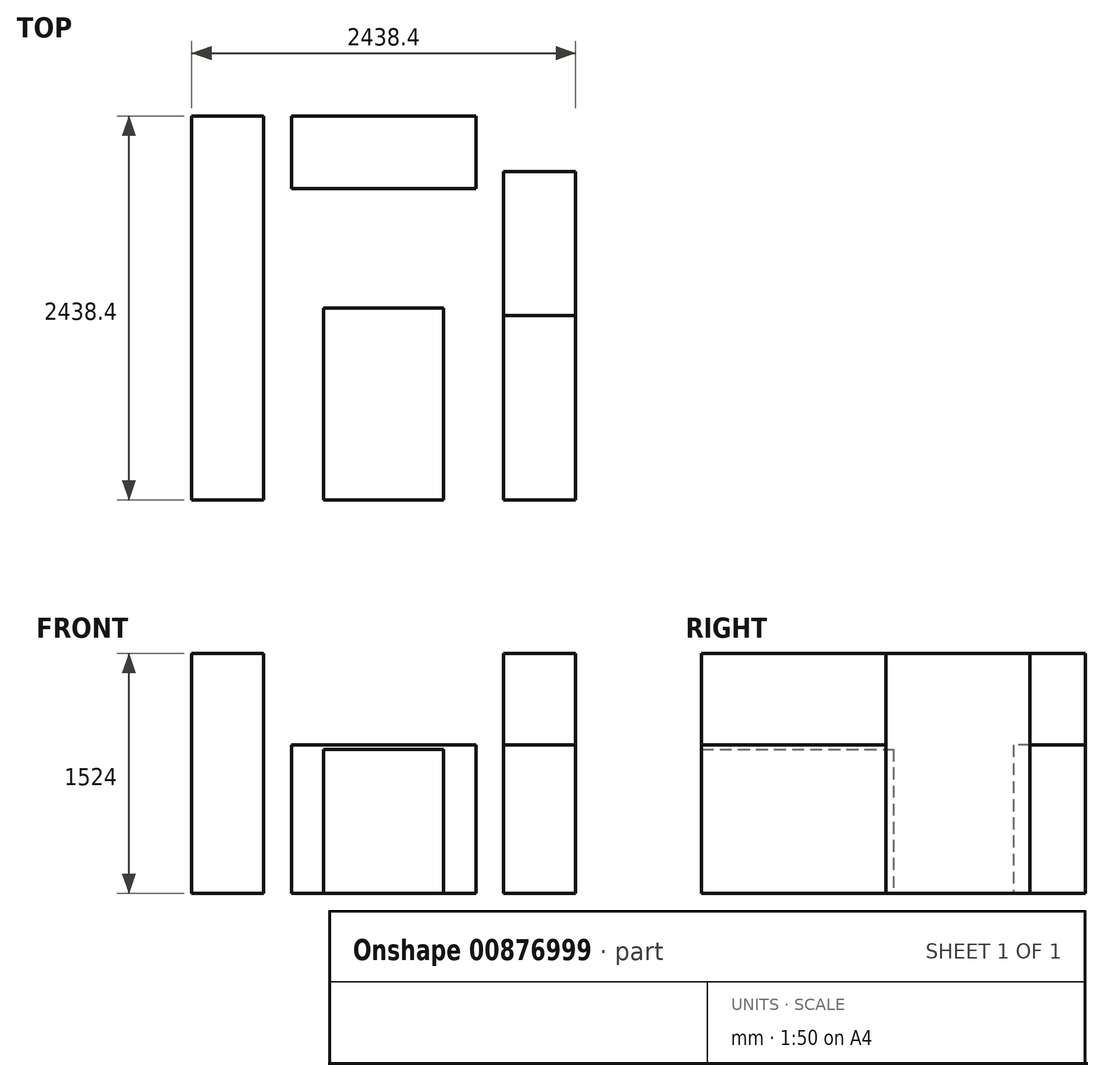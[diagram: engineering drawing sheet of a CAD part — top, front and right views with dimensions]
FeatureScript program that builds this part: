
annotation { "Feature Type Name" : "Feature", "Feature Type Description" : "" }
export const myFeature = defineFeature(function(context is Context, id is Id, definition is map)
    precondition{}
    {
        {
            var Q0;
            Q0=qCreatedBy(makeId("Top.planeOp"),FACE);
            var sketch = newSketch(context, id + "F0", { "sketchPlane" : qUnion([Q0])});
            skLineSegment(sketch, "E0", {"start": v(0, 0) * mm, "end": v(-2438.4, 0) * mm, "construction": true});
            skLineSegment(sketch, "E1.bottom", {"start": v(-2438.4, 0) * mm, "end": v(-1981.2, 0) * mm});
            skLineSegment(sketch, "E1.top", {"start": v(-2438.4, 914.4) * mm, "end": v(-1981.2, 914.4) * mm});
            skLineSegment(sketch, "E1.left", {"start": v(-2438.4, 0) * mm, "end": v(-2438.4, 914.4) * mm});
            skLineSegment(sketch, "E1.right", {"start": v(-1981.2, 0) * mm, "end": v(-1981.2, 914.4) * mm});
            skSolve(sketch);
        }
        {
            var Q0;
            Q0 = qSketchRegion(id + "F0", true);
            extrude(context, id + "F1", {"entities" : qUnion([Q0]), "depth" : 1524 * mm, "offsetDistance" : 25.4 * mm});
        }
        {
            var Q0;
            Q0=qCreatedBy(makeId("Top.planeOp"),FACE);
            var sketch = newSketch(context, id + "F2", { "sketchPlane" : qUnion([Q0])});
            skLineSegment(sketch, "E2", {"start": v(0, 0) * mm, "end": v(-2438.4, 0) * mm, "construction": true});
            skLineSegment(sketch, "E3", {"start": v(-2438.4, 0) * mm, "end": v(-2438.4, 914.4) * mm, "construction": true});
            skLineSegment(sketch, "E4.bottom", {"start": v(-2438.4, 914.4) * mm, "end": v(-1981.2, 914.4) * mm});
            skLineSegment(sketch, "E4.top", {"start": v(-2438.4, 2438.4) * mm, "end": v(-1981.2, 2438.4) * mm});
            skLineSegment(sketch, "E4.left", {"start": v(-2438.4, 914.4) * mm, "end": v(-2438.4, 2438.4) * mm});
            skLineSegment(sketch, "E4.right", {"start": v(-1981.2, 914.4) * mm, "end": v(-1981.2, 2438.4) * mm});
            skSolve(sketch);
        }
        {
            var Q0;
            Q0 = qSketchRegion(id + "F2", true);
            extrude(context, id + "F3", {"entities" : qUnion([Q0]), "operationType" : NewBodyOperationType.ADD, "depth" : 1524 * mm, "offsetDistance" : 25.4 * mm});
        }
        {
            var Q0;
            Q0=qCreatedBy(makeId("Top.planeOp"),FACE);
            var sketch = newSketch(context, id + "F4", { "sketchPlane" : qUnion([Q0])});
            skLineSegment(sketch, "E5.bottom", {"start": v(0, 0) * mm, "end": v(-459.74, 0) * mm});
            skLineSegment(sketch, "E5.top", {"start": v(0, 1170.94) * mm, "end": v(-459.74, 1170.94) * mm});
            skLineSegment(sketch, "E5.left", {"start": v(0, 0) * mm, "end": v(0, 1170.94) * mm});
            skLineSegment(sketch, "E5.right", {"start": v(-459.74, 0) * mm, "end": v(-459.74, 1170.94) * mm});
            skSolve(sketch);
        }
        {
            var Q0;
            Q0 = qSketchRegion(id + "F4", true);
            extrude(context, id + "F5", {"entities" : qUnion([Q0]), "depth" : 942.34 * mm, "offsetDistance" : 25.4 * mm});
        }
        {
            var Q0;
            Q0=qCreatedBy(makeId("Top.planeOp"),FACE);
            var sketch = newSketch(context, id + "F6", { "sketchPlane" : qUnion([Q0])});
            skLineSegment(sketch, "E6", {"start": v(0, 0) * mm, "end": v(-1219.2, 0) * mm, "construction": true});
            skLineSegment(sketch, "E7", {"start": v(-1219.2, 0) * mm, "end": v(-838.2, 0) * mm, "construction": true});
            skLineSegment(sketch, "E8.bottom", {"start": v(-838.2, 0) * mm, "end": v(-1600.2, 0) * mm});
            skLineSegment(sketch, "E8.top", {"start": v(-838.2, 1219.2) * mm, "end": v(-1600.2, 1219.2) * mm});
            skLineSegment(sketch, "E8.left", {"start": v(-838.2, 0) * mm, "end": v(-838.2, 1219.2) * mm});
            skLineSegment(sketch, "E8.right", {"start": v(-1600.2, 0) * mm, "end": v(-1600.2, 1219.2) * mm});
            skSolve(sketch);
        }
        {
            var Q0;
            Q0 = qSketchRegion(id + "F6", true);
            extrude(context, id + "F7", {"entities" : qUnion([Q0]), "depth" : 914.4 * mm, "offsetDistance" : 25.4 * mm});
        }
        {
            var Q0;
            Q0=qCreatedBy(makeId("Top.planeOp"),FACE);
            var sketch = newSketch(context, id + "F8", { "sketchPlane" : qUnion([Q0])});
            skLineSegment(sketch, "E9", {"start": v(0, 0) * mm, "end": v(-1219.2, 0) * mm, "construction": true});
            skLineSegment(sketch, "E10", {"start": v(-1219.2, 0) * mm, "end": v(-1219.2, 2438.4) * mm, "construction": true});
            skLineSegment(sketch, "E11", {"start": v(-1219.2, 2438.4) * mm, "end": v(-633.73, 2438.4) * mm, "construction": true});
            skLineSegment(sketch, "E12.bottom", {"start": v(-633.73, 2438.4) * mm, "end": v(-1804.67, 2438.4) * mm});
            skLineSegment(sketch, "E12.top", {"start": v(-633.73, 1978.66) * mm, "end": v(-1804.67, 1978.66) * mm});
            skLineSegment(sketch, "E12.left", {"start": v(-633.73, 2438.4) * mm, "end": v(-633.73, 1978.66) * mm});
            skLineSegment(sketch, "E12.right", {"start": v(-1804.67, 2438.4) * mm, "end": v(-1804.67, 1978.66) * mm});
            skSolve(sketch);
        }
        {
            var Q0;
            Q0 = qSketchRegion(id + "F8", true);
            extrude(context, id + "F9", {"entities" : qUnion([Q0]), "depth" : 942.34 * mm, "offsetDistance" : 25.4 * mm});
        }
        {
            var Q0;
            Q0=qCreatedBy(makeId("Top.planeOp"),FACE);
            var sketch = newSketch(context, id + "F10", { "sketchPlane" : qUnion([Q0])});
            skLineSegment(sketch, "E13", {"start": v(0, 0) * mm, "end": v(0, 1170.94) * mm, "construction": true});
            skLineSegment(sketch, "E14.bottom", {"start": v(0, 1170.94) * mm, "end": v(-457.2, 1170.94) * mm});
            skLineSegment(sketch, "E14.top", {"start": v(0, 2085.34) * mm, "end": v(-457.2, 2085.34) * mm});
            skLineSegment(sketch, "E14.left", {"start": v(0, 1170.94) * mm, "end": v(0, 2085.34) * mm});
            skLineSegment(sketch, "E14.right", {"start": v(-457.2, 1170.94) * mm, "end": v(-457.2, 2085.34) * mm});
            skSolve(sketch);
        }
        {
            var Q0;
            Q0 = qSketchRegion(id + "F10", true);
            extrude(context, id + "F11", {"entities" : qUnion([Q0]), "depth" : 1524 * mm, "offsetDistance" : 25.4 * mm});
        }
    });
